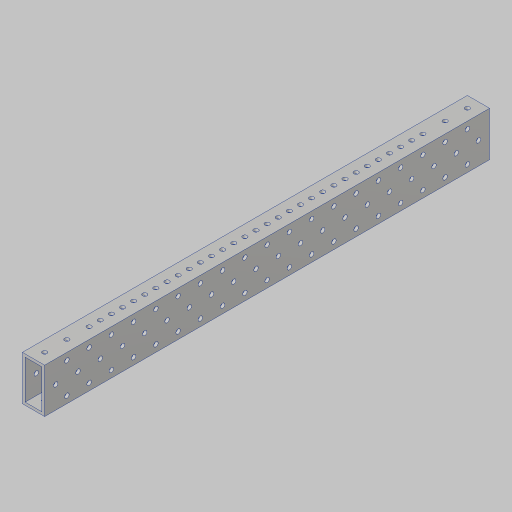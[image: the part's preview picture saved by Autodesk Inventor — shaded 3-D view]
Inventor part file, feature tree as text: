
AUTODESK INVENTOR PART (.ipt)
format: ipt  version: 2023.5 (Build 275446000, 446)  size: 453,120 bytes
history: native  units: in
note: dims shown in document units (in); Inventor stores cm internally (conversion verified against a paired STEP export)
features: hole x2, sketch x2, extrude x1, projected_geometry x1
ambient origin geometry x8: Origin, YZ Plane, XZ Plane, XY Plane, X Axis, Y Axis, Z Axis, Center Point
bodies: Solid1 (feature_tree)
feature tree (6):
  extrude  "Extrusion1"  Depth=0.5in
  hole  "Hole1"  [1 undecoded]
  hole  "Hole2"  [1 undecoded]
  sketch  "Sketch2"  dims[d4=0.0in d5=0.5in]
  sketch  "Sketch3"  dims[d6=1.0in d7=1.0in d8=1.0in d9=5.5118in d11=0.5in d12=0.3937in d14=1.0in d16=5.5118in d18=0.5in d19=0.3937in d21=1.0in d23=0.201in d24=0.75in d25=0.385in d26=0.25in d27=0.5635in d28=0.0055in d29=0.8108in d31=0.5in d33=0.375in d34=0.375in d35=0.5in d36=3.937in d38=1.0in d39=0.3937in d41=1.0in d43=3.937in d45=1.0in d46=0.3937in d48=1.0in d50=0.201in d51=0.75in d52=0.375in d53=0.25in d54=0.5635in d55=1.0in d56=0.8108in]
  projected_geometry  "Projected Loop1"
note: 2 required parameter values undecoded (feature->parameter linkage not recoverable at this tier; creation-order binding heuristic only, values carry confidence <= 0.55)
